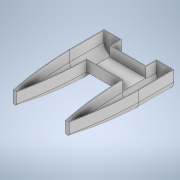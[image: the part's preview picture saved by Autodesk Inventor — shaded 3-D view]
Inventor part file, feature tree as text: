
AUTODESK INVENTOR PART (.ipt)
format: ipt  version: 2020.3 (Build 243373000, 373)  size: 415,232 bytes
history: native  units: mm
features: plane x6, sketch x4, extrude x2, loft x1, chamfer x1, mirror x1, shell x1, other x1, projected_geometry x1
ambient origin geometry x8: Origin, YZ Plane, XZ Plane, XY Plane, X Axis, Y Axis, Z Axis, Center Point
bodies: Solid1 (feature_tree)
feature tree (18):
  sketch  "Sketch1"  dims[d0=100.0mm d1=240.0mm]
  plane  "Work Plane1"
  plane  "Work Plane2"
  plane  "Work Plane3"
  plane  "Work Plane4"
  extrude  "Extrusion1"  Depth=240.0mm
  loft  "Loft3"
  chamfer  "Chamfer1"  Distance=18.0mm
  plane  "Work Plane7"
  mirror  "Mirror1"
  extrude  "Extrusion2"  Depth=25.0mm
  shell  "Shell1"  Thickness=18.0mm
  sketch  "Sketch3"  dims[d2=280.0mm d3=30.0mm]
  sketch  "Sketch4"  dims[d4=50.0mm]
  other  "Edges3"
  plane  "Work Plane5"
  sketch  "Sketch5"  dims[d5=30.0mm d7=18.0mm d8=25.0mm d9=18.0mm d10=25.0mm d11=10.0mm d12=0.0mm d13=25.0mm d14=13.217565mm d16=7.930539mm d17=12.5mm d18=12.5mm d19=7.930539mm d24=10.0mm d25=5.0mm d26=3.0mm d27=3.0mm d28=5.0mm d29=5.0mm d35=0.0mm d36=90.0deg d37=0.0mm d38=90.0deg d39=0.0mm d40=90.0deg d42=2.0mm d43=2.0mm d44=45.0deg d46=-100.0mm d47=30.0mm d48=10.0mm d49=0.0mm d50=2.0mm]
  projected_geometry  "Projected Loop2"
